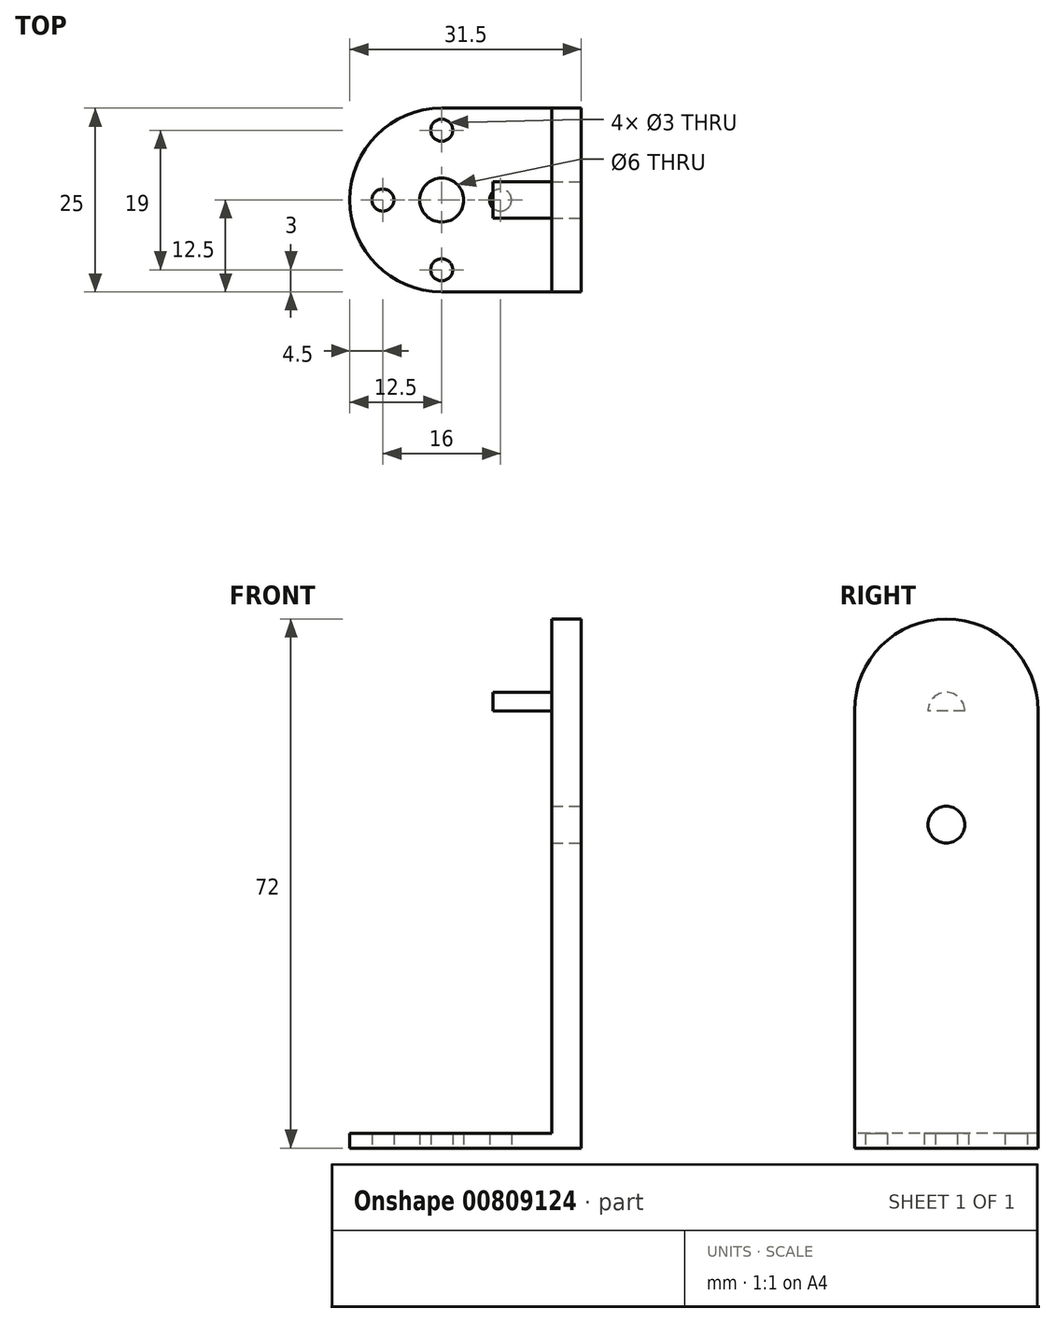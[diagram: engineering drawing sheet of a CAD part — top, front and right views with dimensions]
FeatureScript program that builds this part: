
annotation { "Feature Type Name" : "Feature", "Feature Type Description" : "" }
export const myFeature = defineFeature(function(context is Context, id is Id, definition is map)
    precondition{}
    {
        {
            var Q0;
            Q0=qCreatedBy(makeId("Top.planeOp"),FACE);
            var sketch = newSketch(context, id + "F0", { "sketchPlane" : qUnion([Q0])});
            skPoint(sketch, "E0.middle", {"position": v(0, 0) * mm});
            skCircle(sketch, "E1", {"center": v(0, 0) * mm, "radius": 9.5 * mm});
            skCircle(sketch, "E2", {"center": v(0, 0) * mm, "radius": 8 * mm});
            skCircle(sketch, "E3", {"center": v(0, -9.5) * mm, "radius": 1.5 * mm});
            skCircle(sketch, "E4", {"center": v(-8, 0) * mm, "radius": 1.5 * mm});
            skCircle(sketch, "E5", {"center": v(8, 0) * mm, "radius": 1.5 * mm});
            skCircle(sketch, "E6", {"center": v(0, 0) * mm, "radius": 12.5 * mm});
            skCircle(sketch, "E7", {"center": v(0, 0) * mm, "radius": 3 * mm});
            skCircle(sketch, "E8", {"center": v(0, 9.5) * mm, "radius": 1.5 * mm});
            skLineSegment(sketch, "E9", {"start": v(0, 12.5) * mm, "end": v(19, 12.5) * mm});
            skLineSegment(sketch, "E10", {"start": v(19, 12.5) * mm, "end": v(19, -12.5) * mm});
            skLineSegment(sketch, "E11", {"start": v(19, -12.5) * mm, "end": v(0, -12.5) * mm});
            skSolve(sketch);
        }
        {
            var Q0;
            Q0=makeQuery(id+"F0.imprint","IMPRINT",FACE,{"disambiguationData":[TD([[makeQuery(id+"F0.imprint","IMPRINT",EDGE,{"derivedFrom":sQuery(id+"F0.wireOp",EDGE,"E6")}),1.0]])]});
            var Q1;
            {var subQ0=sQuery(id+"F0.wireOp",EDGE,"PB5VHjtn-gHTu-7EB1-5jxL-tvkM96rimPre");var subQ1=sQuery(id+"F0.wireOp",EDGE,"E1");var subQ2=makeQuery(id+"F0.imprint","INTERSECT",VERTEX,{"disambiguationData":[OD(0.0)],"derivedFrom":[subQ1,subQ0]});Q1=makeQuery(id+"F0.imprint","IMPRINT",FACE,{"disambiguationData":[TD([[makeQuery(id+"F0.imprint","IMPRINT",EDGE,{"disambiguationData":[TD([[subQ2,1.0]])],"derivedFrom":subQ1}),1.0]])]});}
            var Q2;
            {var subQ0=sQuery(id+"F0.wireOp",EDGE,"PB5VHjtn-gHTu-7EB1-5jxL-tvkM96rimPre");var subQ1=sQuery(id+"F0.wireOp",EDGE,"E1");var subQ2=makeQuery(id+"F0.imprint","INTERSECT",VERTEX,{"disambiguationData":[OD(1.0)],"derivedFrom":[subQ1,subQ0]});Q2=makeQuery(id+"F0.imprint","IMPRINT",FACE,{"disambiguationData":[TD([[makeQuery(id+"F0.imprint","IMPRINT",EDGE,{"disambiguationData":[TD([[subQ2,-1.0]])],"derivedFrom":subQ1}),1.0]])]});}
            var Q3;
            {var subQ0=sQuery(id+"F0.wireOp",EDGE,"E4");var subQ1=sQuery(id+"F0.wireOp",EDGE,"E1");var subQ2=makeQuery(id+"F0.imprint","INTERSECT",VERTEX,{"derivedFrom":[subQ1,subQ0]});Q3=makeQuery(id+"F0.imprint","IMPRINT",FACE,{"disambiguationData":[TD([[makeQuery(id+"F0.imprint","IMPRINT",EDGE,{"disambiguationData":[TD([[subQ2,-1.0]])],"derivedFrom":subQ1}),1.0]])]});}
            var Q4;
            {var subQ0=sQuery(id+"F0.wireOp",EDGE,"E5");var subQ1=sQuery(id+"F0.wireOp",EDGE,"E1");var subQ2=makeQuery(id+"F0.imprint","INTERSECT",VERTEX,{"derivedFrom":[subQ1,subQ0]});Q4=makeQuery(id+"F0.imprint","IMPRINT",FACE,{"disambiguationData":[TD([[makeQuery(id+"F0.imprint","IMPRINT",EDGE,{"disambiguationData":[TD([[subQ2,1.0]])],"derivedFrom":subQ1}),1.0]])]});}
            var Q5;
            {var subQ0=sQuery(id+"F0.wireOp",EDGE,"E2");var subQ7=makeQuery(id+"F0.imprint","INTERSECT",VERTEX,{"derivedFrom":[subQ0,sQuery(id+"F0.wireOp",EDGE,"PB5VHjtn-gHTu-7EB1-5jxL-tvkM96rimPre")]});Q5=makeQuery(id+"F0.imprint","IMPRINT",FACE,{"disambiguationData":[TD([[makeQuery(id+"F0.imprint","IMPRINT",EDGE,{"disambiguationData":[TD([[subQ7,1.0]])],"derivedFrom":subQ0}),1.0]])]});}
            var Q6;
            {var subQ0=sQuery(id+"F0.wireOp",EDGE,"E8");var subQ1=sQuery(id+"F0.wireOp",EDGE,"E1");var subQ2=makeQuery(id+"F0.imprint","INTERSECT",VERTEX,{"disambiguationData":[OD(1.0)],"derivedFrom":[subQ1,subQ0]});Q6=makeQuery(id+"F0.imprint","IMPRINT",FACE,{"disambiguationData":[TD([[makeQuery(id+"F0.imprint","IMPRINT",EDGE,{"disambiguationData":[TD([[subQ2,-1.0]])],"derivedFrom":subQ1}),1.0]])]});}
            var Q7;
            {var subQ0=sQuery(id+"F0.wireOp",EDGE,"E8");var subQ1=sQuery(id+"F0.wireOp",EDGE,"E1");var subQ2=makeQuery(id+"F0.imprint","INTERSECT",VERTEX,{"disambiguationData":[OD(0.0)],"derivedFrom":[subQ1,subQ0]});Q7=makeQuery(id+"F0.imprint","IMPRINT",FACE,{"disambiguationData":[TD([[makeQuery(id+"F0.imprint","IMPRINT",EDGE,{"disambiguationData":[TD([[subQ2,1.0]])],"derivedFrom":subQ1}),1.0]])]});}
            var Q8;
            {var subQ0=sQuery(id+"F0.wireOp",EDGE,"E9");Q8=makeQuery(id+"F0.imprint","IMPRINT",FACE,{"disambiguationData":[TD([[makeQuery(id+"F0.imprint","IMPRINT",EDGE,{"derivedFrom":subQ0}),-1.0]])]});}
            extrude(context, id + "F1", {"entities" : qUnion([Q0, Q1, Q2, Q3, Q4, Q5, Q6, Q7, Q8]), "depth" : 2 * mm, "offsetDistance" : 25.4 * mm});
        }
        {
            var Q0;
            Q0=makeQuery(id+"F1.opExtrude","CAP_FACE",FACE,{"disambiguationData":[OSD([sQuery(id+"F0.wireOp",EDGE,"E3"),sQuery(id+"F0.wireOp",EDGE,"E4"),sQuery(id+"F0.wireOp",EDGE,"E5"),sQuery(id+"F0.wireOp",EDGE,"E6"),sQuery(id+"F0.wireOp",EDGE,"E7"),sQuery(id+"F0.wireOp",EDGE,"E8"),sQuery(id+"F0.wireOp",EDGE,"E9"),sQuery(id+"F0.wireOp",EDGE,"E10"),sQuery(id+"F0.wireOp",EDGE,"E11")])],"isStart":false});
            var sketch = newSketch(context, id + "F2", { "sketchPlane" : qUnion([Q0])});
            skLineSegment(sketch, "E12", {"start": v(15, 12.5) * mm, "end": v(15, -12.5) * mm});
            skSolve(sketch);
        }
        {
            var Q0;
            Q0=qSketchRegion(id+"F2",true);
            var Q1;
            {var subQ0=sQuery(id+"F2.wireOp",EDGE,"E12");Q1=makeQuery(id+"F2.imprint","IMPRINT",FACE,{"disambiguationData":[TD([[makeQuery(id+"F2.imprint","IMPRINT",EDGE,{"derivedFrom":subQ0}),1.0]])]});}
            extrude(context, id + "F3", {"entities" : qUnion([Q0, Q1]), "operationType" : NewBodyOperationType.ADD, "depth" : 70 * mm, "offsetDistance" : 25.4 * mm});
        }
        {
            var Q0;
            Q0=makeQuery(id+"F3.opExtrude","SWEPT_FACE",FACE,{"disambiguationData":[OSD([sQuery(id+"F2.wireOp",EDGE,"E12")])]});
            var sketch = newSketch(context, id + "F4", { "sketchPlane" : qUnion([Q0])});
            skCircle(sketch, "E13", {"center": v(0, 59.5) * mm, "radius": 2.5 * mm});
            skLineSegment(sketch, "E14", {"start": v(0, 59.5) * mm, "end": v(0, 72) * mm, "construction": true});
            skLineSegment(sketch, "E15", {"start": v(-12.5, 59.5) * mm, "end": v(0, 59.5) * mm, "construction": true});
            skLineSegment(sketch, "E16", {"start": v(-2.5, 59.5) * mm, "end": v(2.5, 59.5) * mm});
            skSolve(sketch);
        }
        {
            var Q0;
            {var subQ0=sQuery(id+"F4.wireOp",EDGE,"E16");Q0=makeQuery(id+"F4.imprint","IMPRINT",FACE,{"disambiguationData":[TD([[makeQuery(id+"F4.imprint","IMPRINT",EDGE,{"derivedFrom":subQ0}),1.0]])]});}
            extrude(context, id + "F5", {"entities" : qUnion([Q0]), "operationType" : NewBodyOperationType.ADD, "depth" : 8 * mm, "offsetDistance" : 25.4 * mm});
        }
        {
            var Q0;
            Q0=makeQuery(id+"F3.opExtrude","CAP_EDGE",EDGE,{"disambiguationData":[OSD([sQuery(id+"F0.wireOp",EDGE,"E11")])],"isStart":false});
            var Q1;
            Q1=makeQuery(id+"F3.opExtrude","CAP_EDGE",EDGE,{"disambiguationData":[OSD([sQuery(id+"F0.wireOp",EDGE,"E9")])],"isStart":false});
            fillet(context, id + "F6", {"entities" : qUnion([Q0, Q1]), "radius" : 12.5 * mm, "tangentPropagation" : true, "allowEdgeOverflow" : false});
        }
        {
            var Q0;
            {var subQ0=sQuery(id+"F0.wireOp",EDGE,"E10");Q0=makeQuery(id+"F3.boolean.opBoolean","MERGE",FACE,{"derivedFrom":[makeQuery(id+"F1.opExtrude","SWEPT_FACE",FACE,{"disambiguationData":[OSD([subQ0])]}),makeQuery(id+"F3.opExtrude","SWEPT_FACE",FACE,{"disambiguationData":[OSD([subQ0])]})]});}
            var sketch = newSketch(context, id + "F7", { "sketchPlane" : qUnion([Q0])});
            skCircle(sketch, "E17", {"center": v(0, 44) * mm, "radius": 2.5 * mm});
            skLineSegment(sketch, "E18", {"start": v(0, 44) * mm, "end": v(0, 72) * mm, "construction": true});
            skSolve(sketch);
        }
        {
            var Q0;
            Q0 = qSketchRegion(id + "F7", true);
            extrude(context, id + "F8", {"entities" : qUnion([Q0]), "operationType" : NewBodyOperationType.REMOVE, "endBound" : BoundingType.UP_TO_NEXT, "oppositeDirection" : true, "depth" : 25.4 * mm, "offsetDistance" : 25.4 * mm});
        }
    });
